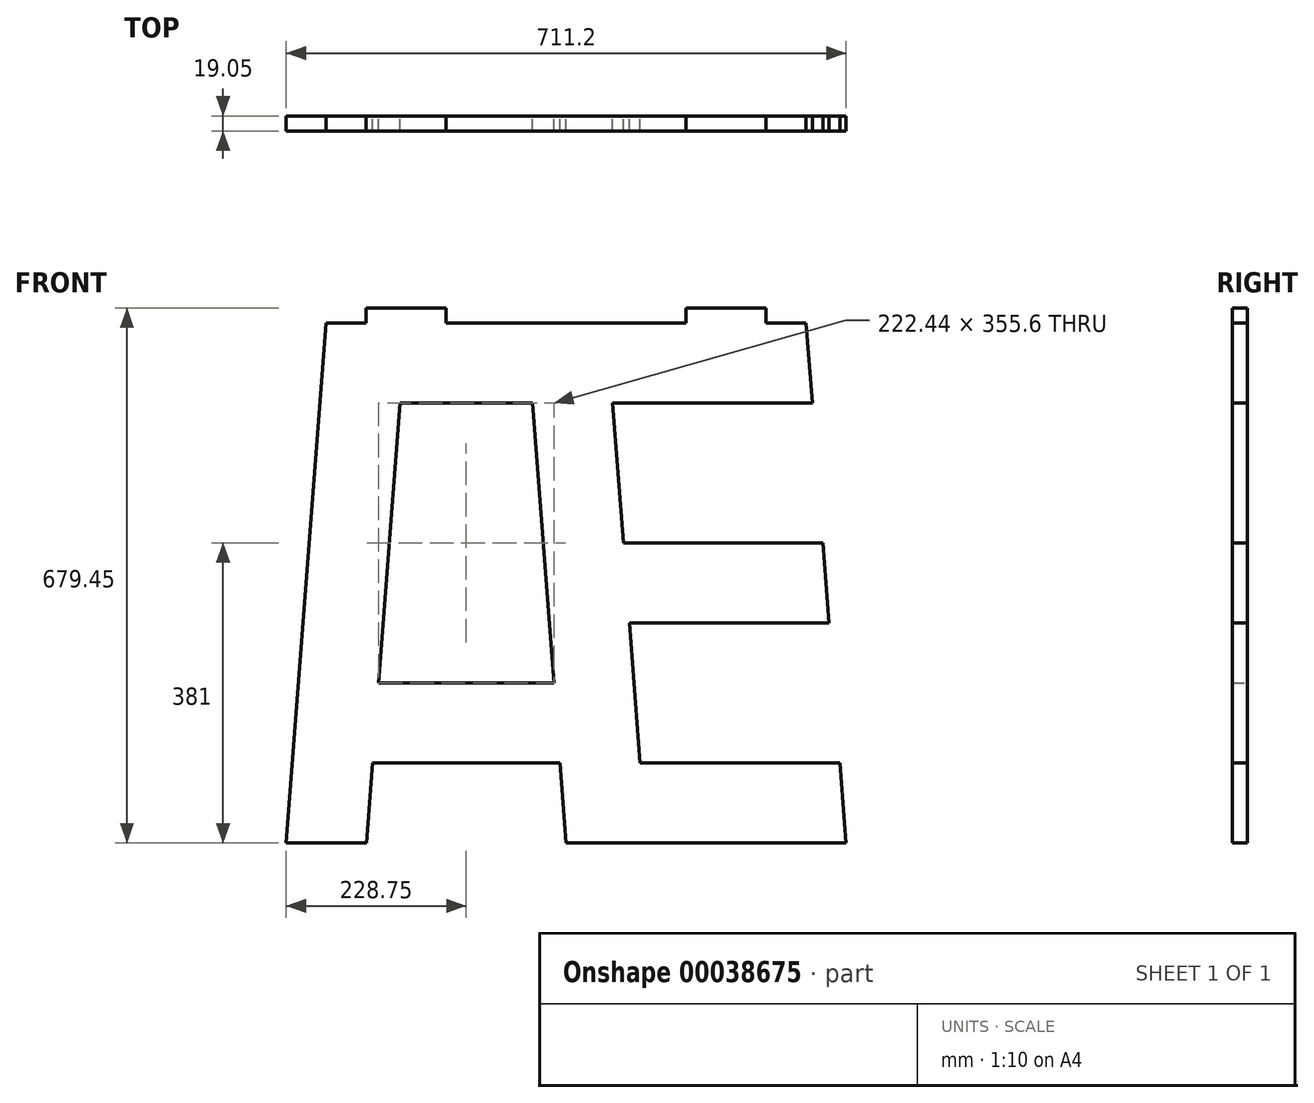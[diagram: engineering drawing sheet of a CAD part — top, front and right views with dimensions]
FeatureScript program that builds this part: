
annotation { "Feature Type Name" : "Feature", "Feature Type Description" : "" }
export const myFeature = defineFeature(function(context is Context, id is Id, definition is map)
    precondition{}
    {
        {
            var Q0;
            Q0=qCreatedBy(makeId("Front.planeOp"),FACE);
            var sketch = newSketch(context, id + "F0", { "sketchPlane" : qUnion([Q0])});
            skLineSegment(sketch, "E0", {"start": v(-304.8, 660.4) * mm, "end": v(-355.6, 0) * mm});
            skLineSegment(sketch, "E1", {"start": v(-355.6, 0) * mm, "end": v(355.6, 0) * mm});
            skLineSegment(sketch, "E2", {"start": v(355.6, 0) * mm, "end": v(304.8, 660.4) * mm});
            skLineSegment(sketch, "E3", {"start": v(304.8, 660.4) * mm, "end": v(-304.8, 660.4) * mm});
            skLineSegment(sketch, "E4", {"start": v(0, 660.4) * mm, "end": v(0, 0) * mm, "construction": true});
            skLineSegment(sketch, "E5", {"start": v(-253.7, 0) * mm, "end": v(-202.9, 660.4) * mm});
            skLineSegment(sketch, "E6", {"start": v(0, 0) * mm, "end": v(-50.8, 660.4) * mm});
            skLineSegment(sketch, "E7", {"start": v(51.1, 660.4) * mm, "end": v(101.9, 0) * mm});
            skLineSegment(sketch, "E8", {"start": v(58.92, 558.8) * mm, "end": v(312.62, 558.8) * mm});
            skLineSegment(sketch, "E9", {"start": v(76.5, 330.2) * mm, "end": v(330.2, 330.2) * mm, "construction": true});
            skLineSegment(sketch, "E10", {"start": v(72.6, 381) * mm, "end": v(326.3, 381) * mm});
            skLineSegment(sketch, "E11", {"start": v(80.4, 279.4) * mm, "end": v(334.1, 279.4) * mm});
            skLineSegment(sketch, "E12", {"start": v(94.08, 101.6) * mm, "end": v(347.78, 101.6) * mm});
            skLineSegment(sketch, "E13", {"start": v(-210.72, 558.8) * mm, "end": v(-42.98, 558.8) * mm});
            skLineSegment(sketch, "E14", {"start": v(-7.82, 101.6) * mm, "end": v(-245.88, 101.6) * mm});
            skLineSegment(sketch, "E15", {"start": v(-238.07, 203.2) * mm, "end": v(-15.63, 203.2) * mm});
            skSolve(sketch);
        }
        {
            var Q0;
            {var subQ0=sQuery(id+"F0.wireOp",EDGE,"E8");Q0=makeQuery(id+"F0.imprint","IMPRINT",FACE,{"disambiguationData":[TD([[makeQuery(id+"F0.imprint","IMPRINT",EDGE,{"derivedFrom":subQ0}),1.0]])]});}
            var Q1;
            {var subQ0=sQuery(id+"F0.wireOp",EDGE,"E12");Q1=makeQuery(id+"F0.imprint","IMPRINT",FACE,{"disambiguationData":[TD([[makeQuery(id+"F0.imprint","IMPRINT",EDGE,{"derivedFrom":subQ0}),-1.0]])]});}
            var Q2;
            {var subQ1=sQuery(id+"F0.wireOp",EDGE,"E14");Q2=makeQuery(id+"F0.imprint","IMPRINT",FACE,{"disambiguationData":[TD([[makeQuery(id+"F0.imprint","IMPRINT",EDGE,{"derivedFrom":subQ1}),-1.0]])]});}
            var Q3;
            {var subQ1=sQuery(id+"F0.wireOp",EDGE,"E10");Q3=makeQuery(id+"F0.imprint","IMPRINT",FACE,{"disambiguationData":[TD([[makeQuery(id+"F0.imprint","IMPRINT",EDGE,{"derivedFrom":subQ1}),-1.0]])]});}
            var Q4;
            {var subQ4=sQuery(id+"F0.wireOp",EDGE,"E0");Q4=makeQuery(id+"F0.imprint","IMPRINT",FACE,{"disambiguationData":[TD([[makeQuery(id+"F0.imprint","IMPRINT",EDGE,{"derivedFrom":subQ4}),1.0]])]});}
            var Q5;
            {var subQ2=sQuery(id+"F0.wireOp",EDGE,"E1");var subQ6=sQuery(id+"F0.wireOp",EDGE,"E6");var subQ9=makeQuery(id+"F0.imprint","INTERSECT",VERTEX,{"derivedFrom":[subQ2,subQ6]});Q5=makeQuery(id+"F0.imprint","IMPRINT",FACE,{"disambiguationData":[TD([[makeQuery(id+"F0.imprint","IMPRINT",EDGE,{"disambiguationData":[TD([[subQ9,-1.0]])],"derivedFrom":subQ2}),1.0]])]});}
            var Q6;
            {var subQ0=sQuery(id+"F0.wireOp",EDGE,"E13");Q6=makeQuery(id+"F0.imprint","IMPRINT",FACE,{"disambiguationData":[TD([[makeQuery(id+"F0.imprint","IMPRINT",EDGE,{"derivedFrom":subQ0}),1.0]])]});}
            extrude(context, id + "F1", {"entities" : qUnion([Q0, Q1, Q2, Q3, Q4, Q5, Q6]), "depth" : 19.05 * mm});
        }
        {
            var Q0;
            Q0=makeQuery(id+"F1.opExtrude","CAP_FACE",FACE,{"disambiguationData":[OSD([sQuery(id+"F0.wireOp",EDGE,"E0"),sQuery(id+"F0.wireOp",EDGE,"E1"),sQuery(id+"F0.wireOp",EDGE,"E2"),sQuery(id+"F0.wireOp",EDGE,"E3"),sQuery(id+"F0.wireOp",EDGE,"E5"),sQuery(id+"F0.wireOp",EDGE,"E6"),sQuery(id+"F0.wireOp",EDGE,"E7"),sQuery(id+"F0.wireOp",EDGE,"E8"),sQuery(id+"F0.wireOp",EDGE,"E10"),sQuery(id+"F0.wireOp",EDGE,"E11"),sQuery(id+"F0.wireOp",EDGE,"E12"),sQuery(id+"F0.wireOp",EDGE,"E13"),sQuery(id+"F0.wireOp",EDGE,"E14"),sQuery(id+"F0.wireOp",EDGE,"E15")])],"isStart":false});
            var sketch = newSketch(context, id + "F2", { "sketchPlane" : qUnion([Q0])});
            skLineSegment(sketch, "E16.bottom", {"start": v(-254, 660.4) * mm, "end": v(-152.4, 660.4) * mm});
            skLineSegment(sketch, "E16.top", {"start": v(-254, 679.45) * mm, "end": v(-152.4, 679.45) * mm});
            skLineSegment(sketch, "E16.left", {"start": v(-254, 660.4) * mm, "end": v(-254, 679.45) * mm});
            skLineSegment(sketch, "E16.right", {"start": v(-152.4, 660.4) * mm, "end": v(-152.4, 679.45) * mm});
            skLineSegment(sketch, "E17.bottom", {"start": v(152.4, 660.4) * mm, "end": v(254, 660.4) * mm});
            skLineSegment(sketch, "E17.top", {"start": v(152.4, 679.45) * mm, "end": v(254, 679.45) * mm});
            skLineSegment(sketch, "E17.left", {"start": v(152.4, 660.4) * mm, "end": v(152.4, 679.45) * mm});
            skLineSegment(sketch, "E17.right", {"start": v(254, 660.4) * mm, "end": v(254, 679.45) * mm});
            skLineSegment(sketch, "E18", {"start": v(-152.4, 679.45) * mm, "end": v(152.4, 679.45) * mm, "construction": true});
            skLineSegment(sketch, "E19", {"start": v(0, 679.45) * mm, "end": v(0, 660.4) * mm});
            skSolve(sketch);
        }
        {
            var Q0;
            Q0=makeQuery(id+"F2.imprint","IMPRINT",FACE,{"disambiguationData":[TD([[makeQuery(id+"F2.imprint","IMPRINT",EDGE,{"derivedFrom":sQuery(id+"F2.wireOp",EDGE,"E17.bottom")}),-1.0]])]});
            var Q1;
            Q1=makeQuery(id+"F2.imprint","IMPRINT",FACE,{"disambiguationData":[TD([[makeQuery(id+"F2.imprint","IMPRINT",EDGE,{"derivedFrom":sQuery(id+"F2.wireOp",EDGE,"E16.bottom")}),-1.0]])]});
            var Q2;
            Q2=makeQuery(id+"F1.opExtrude","CAP_FACE",FACE,{"disambiguationData":[OSD([sQuery(id+"F0.wireOp",EDGE,"E0"),sQuery(id+"F0.wireOp",EDGE,"E1"),sQuery(id+"F0.wireOp",EDGE,"E2"),sQuery(id+"F0.wireOp",EDGE,"E3"),sQuery(id+"F0.wireOp",EDGE,"E5"),sQuery(id+"F0.wireOp",EDGE,"E6"),sQuery(id+"F0.wireOp",EDGE,"E7"),sQuery(id+"F0.wireOp",EDGE,"E8"),sQuery(id+"F0.wireOp",EDGE,"E10"),sQuery(id+"F0.wireOp",EDGE,"E11"),sQuery(id+"F0.wireOp",EDGE,"E12"),sQuery(id+"F0.wireOp",EDGE,"E13"),sQuery(id+"F0.wireOp",EDGE,"E14"),sQuery(id+"F0.wireOp",EDGE,"E15")])],"isStart":true});
            extrude(context, id + "F3", {"entities" : qUnion([Q0, Q1]), "operationType" : NewBodyOperationType.ADD, "endBound" : BoundingType.UP_TO_SURFACE, "oppositeDirection" : true, "endBoundEntityFace" : qUnion([Q2]), "depth" : 25.4 * mm});
        }
    });
